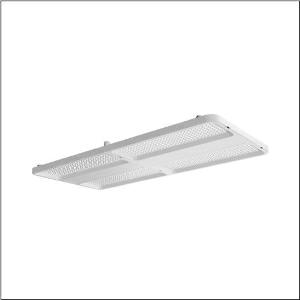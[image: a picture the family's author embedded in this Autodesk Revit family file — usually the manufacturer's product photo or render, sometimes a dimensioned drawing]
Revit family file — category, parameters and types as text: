
# Revit family: highbay_21_maxi_52hn12db3lda
name_source: partatom
category: Lighting Fixtures
units: mm (PartAtom-declared; Revit-internal decimal feet)

## family parameters
Cut with Voids When Loaded = No
Host = Face
Light Source = No
Part Type = Normal
Room Calculation Point = No
Round Connector Dimension = Use Diameter
Shared = No

## types (1)
- --- (1 x LED, 3880 lm, 22.6 W, 3000K)
    Apparent Load = 23 VA
    CIE Flux Codes = 90 98 100 100 100
    Color Rendering = 80
    Color Temperature = 3000K
    Default Elevation = 1800 mm
    Description = high bay luminaire Highbay 21 maxi; direct symmetric wide distribution, light control with lens of PMMA; UGR ≤ 22 (X = 4H | Y = 8H | S = 0.25H | reflection values 70/50/20); luminous flux: 25.590lm; light colour: 830, colour temperature: 3000K, MacAdam ≤ 3 SDCM (initial), colour rendering: CRI > 80; luminous efficacy: 177,7lm/W; rated service life: 75.000h (L80) at AT= ta max; control: DALI 2; luminaire connection: terminal, 5-pole, max. 2.5mm² (cable entry for one cable, Ø 8.5..16mm); mains connection: 230..240V, AC/DC 0/50..60Hz; connected load: 144W; protection rating (complete): IP66; insulation class (complete): insulation class I (protective earthing); protection symbol: D; impact resistance: IK08; certification: CE, ENEC, VDE, UKCA; luminaire for central battery installations according to EN 60598-2-22, internal wiring halogen-free; luminaire LABS conformity tested according to VDMA 24364:2018-05; Suitable for use in the food industry according to the specifications of IFS-Food, HACCP and/or BRC; housing frame of high-performance plastic PA6, matt traffic white (RAL 9016); cover of PMMA; dimension (LxWxH): 946 x 442 x 72mm; permissible operating ambient temperature: -40..+65°C (reducing of maximum allowable ambient temperature of 5°C with ceiling mounting); packaging unit: 1 piece; (delivery without accessories; please order mounting accessories separately)
    Height = 72 mm  [stored 0.23622 ft]
    Lamp = 1 x LED
    Lamp Light Flux = 3880 lm
    Lamp Power = 22.6 W
    Lamp count = 1
    Length = 946 mm
    Luminous efficacy = 172 lm/W
    Manufacturer = Siteco
    ModVariant = No
    Model = 52HN12DB3LDA
    Mounting Place = Ceiling
    Mounting Type = Pendant
    Number of Poles = 1
    OnlyDefault = Yes
    Power Factor = 1
    Product Name = Highbay 21 maxi
    Product group = high bay luminaire
    ProductGroupID = 902
    Protection Class = Protection class I
    Protection Degree = IP 66
    RLX_Detail_Level = 1
    RLX_Emergency_Light_Flux = 0 lm
    RLX_Emergency_Type = 0
    RLX_Emergency_Type_DB = No
    RlxData = <blob elided: 127757 chars, md5=bf72c792>
    Socket = socket
    Standby Power = 0 W
    System Light Flux = 3880 lm
    System Power = 23 W
    Type Comments = : DC mode (central or group accumulator) initial emergency light level
    Type Image = l_1363244.jpg
    URL = http://relux.com
    VarID = @adj_004889
    Voltage = 0 V
    Weight = 0.00 kg
    Width = 442 mm

note: [stored X ft] marks values corroborated as IEEE doubles in the binary element streams (Revit-internal decimal feet)

## geometry (parser evidence)
native form markers: Blend x4, Sweep x11
no freeform markers — native parametric forms only
